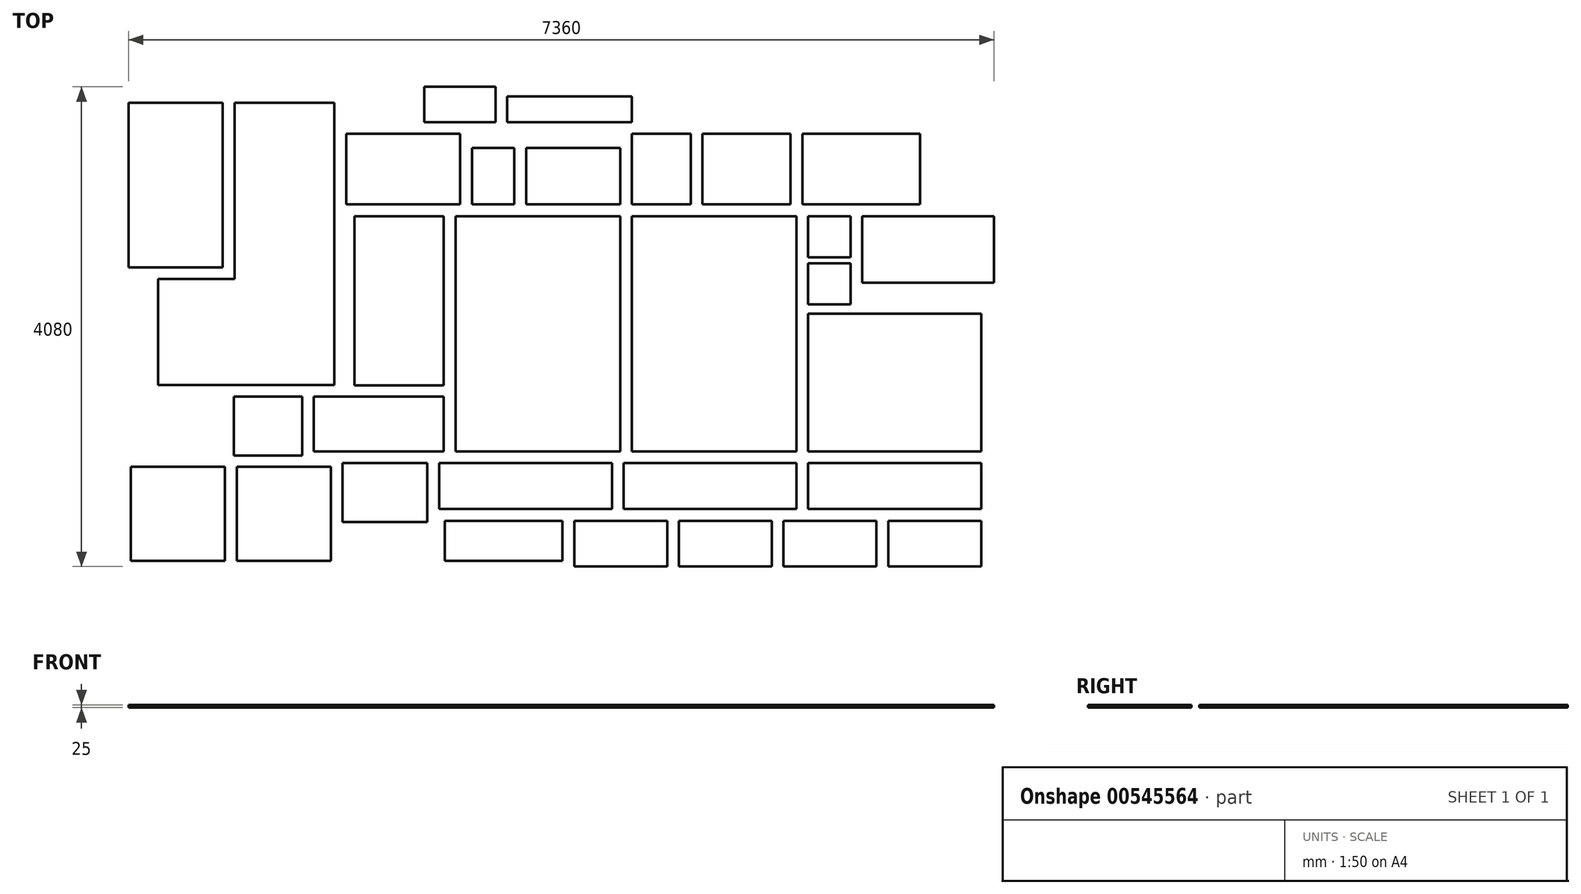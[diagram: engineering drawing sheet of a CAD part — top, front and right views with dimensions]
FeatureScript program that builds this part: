
annotation { "Feature Type Name" : "Feature", "Feature Type Description" : "" }
export const myFeature = defineFeature(function(context is Context, id is Id, definition is map)
    precondition{}
    {
        {
            var Q0;
            Q0=qCreatedBy(makeId("Top.planeOp"),FACE);
            var sketch = newSketch(context, id + "F0", { "sketchPlane" : qUnion([Q0])});
            skLineSegment(sketch, "E0.bottom", {"start": v(0, 0) * mm, "end": v(500, 0) * mm});
            skLineSegment(sketch, "E0.top", {"start": v(0, 600) * mm, "end": v(500, 600) * mm});
            skLineSegment(sketch, "E0.left", {"start": v(0, 0) * mm, "end": v(0, 600) * mm});
            skLineSegment(sketch, "E0.right", {"start": v(500, 0) * mm, "end": v(500, 600) * mm});
            skLineSegment(sketch, "E1.bottom", {"start": v(600, 0) * mm, "end": v(1350, 0) * mm});
            skLineSegment(sketch, "E1.top", {"start": v(600, 600) * mm, "end": v(1350, 600) * mm});
            skLineSegment(sketch, "E1.left", {"start": v(600, 0) * mm, "end": v(600, 600) * mm});
            skLineSegment(sketch, "E1.right", {"start": v(1350, 0) * mm, "end": v(1350, 600) * mm});
            skLineSegment(sketch, "E2.bottom", {"start": v(1450, 0) * mm, "end": v(2450, 0) * mm});
            skLineSegment(sketch, "E2.top", {"start": v(1450, 600) * mm, "end": v(2450, 600) * mm});
            skLineSegment(sketch, "E2.left", {"start": v(1450, 0) * mm, "end": v(1450, 600) * mm});
            skLineSegment(sketch, "E2.right", {"start": v(2450, 0) * mm, "end": v(2450, 600) * mm});
            skLineSegment(sketch, "E3.bottom", {"start": v(0, -100) * mm, "end": v(1400, -100) * mm});
            skLineSegment(sketch, "E3.top", {"start": v(0, -2100) * mm, "end": v(1400, -2100) * mm});
            skLineSegment(sketch, "E3.left", {"start": v(0, -100) * mm, "end": v(0, -2100) * mm});
            skLineSegment(sketch, "E3.right", {"start": v(1400, -100) * mm, "end": v(1400, -2100) * mm});
            skLineSegment(sketch, "E4.bottom", {"start": v(1500, -100) * mm, "end": v(1860, -100) * mm});
            skLineSegment(sketch, "E4.top", {"start": v(1500, -450) * mm, "end": v(1860, -450) * mm});
            skLineSegment(sketch, "E4.left", {"start": v(1500, -100) * mm, "end": v(1500, -450) * mm});
            skLineSegment(sketch, "E4.right", {"start": v(1860, -100) * mm, "end": v(1860, -450) * mm});
            skLineSegment(sketch, "E5.bottom", {"start": v(1500, -500) * mm, "end": v(1860, -500) * mm});
            skLineSegment(sketch, "E5.top", {"start": v(1500, -850) * mm, "end": v(1860, -850) * mm});
            skLineSegment(sketch, "E5.left", {"start": v(1500, -500) * mm, "end": v(1500, -850) * mm});
            skLineSegment(sketch, "E5.right", {"start": v(1860, -500) * mm, "end": v(1860, -850) * mm});
            skLineSegment(sketch, "E6.bottom", {"start": v(-100, -100) * mm, "end": v(-1500, -100) * mm});
            skLineSegment(sketch, "E6.top", {"start": v(-100, -2100) * mm, "end": v(-1500, -2100) * mm});
            skLineSegment(sketch, "E6.left", {"start": v(-100, -100) * mm, "end": v(-100, -2100) * mm});
            skLineSegment(sketch, "E6.right", {"start": v(-1500, -100) * mm, "end": v(-1500, -2100) * mm});
            skLineSegment(sketch, "E7.bottom", {"start": v(1500, -2100) * mm, "end": v(2970, -2100) * mm});
            skLineSegment(sketch, "E7.top", {"start": v(1500, -930) * mm, "end": v(2970, -930) * mm});
            skLineSegment(sketch, "E7.left", {"start": v(1500, -2100) * mm, "end": v(1500, -930) * mm});
            skLineSegment(sketch, "E7.right", {"start": v(2970, -2100) * mm, "end": v(2970, -930) * mm});
            skLineSegment(sketch, "E8.bottom", {"start": v(-100, 480) * mm, "end": v(-900, 480) * mm});
            skLineSegment(sketch, "E8.top", {"start": v(-100, 0) * mm, "end": v(-900, 0) * mm});
            skLineSegment(sketch, "E8.left", {"start": v(-100, 480) * mm, "end": v(-100, 0) * mm});
            skLineSegment(sketch, "E8.right", {"start": v(-900, 480) * mm, "end": v(-900, 0) * mm});
            skLineSegment(sketch, "E9.bottom", {"start": v(-1360, 480) * mm, "end": v(-1000, 480) * mm});
            skLineSegment(sketch, "E9.top", {"start": v(-1360, 0) * mm, "end": v(-1000, 0) * mm});
            skLineSegment(sketch, "E9.left", {"start": v(-1360, 480) * mm, "end": v(-1360, 0) * mm});
            skLineSegment(sketch, "E9.right", {"start": v(-1000, 480) * mm, "end": v(-1000, 0) * mm});
            skLineSegment(sketch, "E10.bottom", {"start": v(-1460, 600) * mm, "end": v(-2430, 600) * mm});
            skLineSegment(sketch, "E10.top", {"start": v(-1460, 0) * mm, "end": v(-2430, 0) * mm});
            skLineSegment(sketch, "E10.left", {"start": v(-1460, 600) * mm, "end": v(-1460, 0) * mm});
            skLineSegment(sketch, "E10.right", {"start": v(-2430, 600) * mm, "end": v(-2430, 0) * mm});
            skLineSegment(sketch, "E11.bottom", {"start": v(-2360, -100) * mm, "end": v(-1600, -100) * mm});
            skLineSegment(sketch, "E11.top", {"start": v(-2360, -1540) * mm, "end": v(-1600, -1540) * mm});
            skLineSegment(sketch, "E11.left", {"start": v(-2360, -100) * mm, "end": v(-2360, -1540) * mm});
            skLineSegment(sketch, "E11.right", {"start": v(-1600, -100) * mm, "end": v(-1600, -1540) * mm});
            skLineSegment(sketch, "E12.bottom", {"start": v(-1600, -2100) * mm, "end": v(-2705, -2100) * mm});
            skLineSegment(sketch, "E12.top", {"start": v(-1600, -1635) * mm, "end": v(-2705, -1635) * mm});
            skLineSegment(sketch, "E12.left", {"start": v(-1600, -2100) * mm, "end": v(-1600, -1635) * mm});
            skLineSegment(sketch, "E12.right", {"start": v(-2705, -2100) * mm, "end": v(-2705, -1635) * mm});
            skLineSegment(sketch, "E13.bottom", {"start": v(0, 920) * mm, "end": v(-1060, 920) * mm});
            skLineSegment(sketch, "E13.top", {"start": v(0, 700) * mm, "end": v(-1060, 700) * mm});
            skLineSegment(sketch, "E13.left", {"start": v(0, 920) * mm, "end": v(0, 700) * mm});
            skLineSegment(sketch, "E13.right", {"start": v(-1060, 920) * mm, "end": v(-1060, 700) * mm});
            skLineSegment(sketch, "E14.bottom", {"start": v(-1765, 1000) * mm, "end": v(-1160, 1000) * mm});
            skLineSegment(sketch, "E14.top", {"start": v(-1765, 700) * mm, "end": v(-1160, 700) * mm});
            skLineSegment(sketch, "E14.left", {"start": v(-1765, 1000) * mm, "end": v(-1765, 700) * mm});
            skLineSegment(sketch, "E14.right", {"start": v(-1160, 1000) * mm, "end": v(-1160, 700) * mm});
            skLineSegment(sketch, "E15.bottom", {"start": v(1960, -100) * mm, "end": v(3080, -100) * mm});
            skLineSegment(sketch, "E15.top", {"start": v(1960, -665) * mm, "end": v(3080, -665) * mm});
            skLineSegment(sketch, "E15.left", {"start": v(1960, -100) * mm, "end": v(1960, -665) * mm});
            skLineSegment(sketch, "E15.right", {"start": v(3080, -100) * mm, "end": v(3080, -665) * mm});
            skLineSegment(sketch, "E16", {"start": v(-2530, -1535) * mm, "end": v(-4030, -1535) * mm});
            skLineSegment(sketch, "E17", {"start": v(-4030, -1535) * mm, "end": v(-4030, -635) * mm});
            skLineSegment(sketch, "E18", {"start": v(-4030, -635) * mm, "end": v(-3380, -635) * mm});
            skLineSegment(sketch, "E19", {"start": v(-3380, -635) * mm, "end": v(-3380, 865) * mm});
            skLineSegment(sketch, "E20", {"start": v(-3380, 865) * mm, "end": v(-2530, 865) * mm});
            skLineSegment(sketch, "E21", {"start": v(-2530, 865) * mm, "end": v(-2530, -1535) * mm});
            skLineSegment(sketch, "E22.bottom", {"start": v(2970, -2200) * mm, "end": v(1500, -2200) * mm});
            skLineSegment(sketch, "E22.top", {"start": v(2970, -2590) * mm, "end": v(1500, -2590) * mm});
            skLineSegment(sketch, "E22.left", {"start": v(2970, -2200) * mm, "end": v(2970, -2590) * mm});
            skLineSegment(sketch, "E22.right", {"start": v(1500, -2200) * mm, "end": v(1500, -2590) * mm});
            skLineSegment(sketch, "E23.bottom", {"start": v(1400, -2200) * mm, "end": v(-70, -2200) * mm});
            skLineSegment(sketch, "E23.top", {"start": v(1400, -2590) * mm, "end": v(-70, -2590) * mm});
            skLineSegment(sketch, "E23.left", {"start": v(1400, -2200) * mm, "end": v(1400, -2590) * mm});
            skLineSegment(sketch, "E23.right", {"start": v(-70, -2200) * mm, "end": v(-70, -2590) * mm});
            skLineSegment(sketch, "E24.bottom", {"start": v(-170, -2200) * mm, "end": v(-1640, -2200) * mm});
            skLineSegment(sketch, "E24.top", {"start": v(-170, -2590) * mm, "end": v(-1640, -2590) * mm});
            skLineSegment(sketch, "E24.left", {"start": v(-170, -2200) * mm, "end": v(-170, -2590) * mm});
            skLineSegment(sketch, "E24.right", {"start": v(-1640, -2200) * mm, "end": v(-1640, -2590) * mm});
            skLineSegment(sketch, "E25.bottom", {"start": v(2970, -2690) * mm, "end": v(2180, -2690) * mm});
            skLineSegment(sketch, "E25.top", {"start": v(2970, -3080) * mm, "end": v(2180, -3080) * mm});
            skLineSegment(sketch, "E25.left", {"start": v(2970, -2690) * mm, "end": v(2970, -3080) * mm});
            skLineSegment(sketch, "E25.right", {"start": v(2180, -2690) * mm, "end": v(2180, -3080) * mm});
            skLineSegment(sketch, "E26.bottom", {"start": v(2080, -2690) * mm, "end": v(1290, -2690) * mm});
            skLineSegment(sketch, "E26.top", {"start": v(2080, -3080) * mm, "end": v(1290, -3080) * mm});
            skLineSegment(sketch, "E26.left", {"start": v(2080, -2690) * mm, "end": v(2080, -3080) * mm});
            skLineSegment(sketch, "E26.right", {"start": v(1290, -2690) * mm, "end": v(1290, -3080) * mm});
            skLineSegment(sketch, "E27.bottom", {"start": v(1190, -2690) * mm, "end": v(400, -2690) * mm});
            skLineSegment(sketch, "E27.top", {"start": v(1190, -3080) * mm, "end": v(400, -3080) * mm});
            skLineSegment(sketch, "E27.left", {"start": v(1190, -2690) * mm, "end": v(1190, -3080) * mm});
            skLineSegment(sketch, "E27.right", {"start": v(400, -2690) * mm, "end": v(400, -3080) * mm});
            skLineSegment(sketch, "E28.bottom", {"start": v(300, -2690) * mm, "end": v(-490, -2690) * mm});
            skLineSegment(sketch, "E28.top", {"start": v(300, -3080) * mm, "end": v(-490, -3080) * mm});
            skLineSegment(sketch, "E28.left", {"start": v(300, -2690) * mm, "end": v(300, -3080) * mm});
            skLineSegment(sketch, "E28.right", {"start": v(-490, -2690) * mm, "end": v(-490, -3080) * mm});
            skLineSegment(sketch, "E29.bottom", {"start": v(-3385, -1635) * mm, "end": v(-2805, -1635) * mm});
            skLineSegment(sketch, "E29.top", {"start": v(-3385, -2135) * mm, "end": v(-2805, -2135) * mm});
            skLineSegment(sketch, "E29.left", {"start": v(-3385, -1635) * mm, "end": v(-3385, -2135) * mm});
            skLineSegment(sketch, "E29.right", {"start": v(-2805, -1635) * mm, "end": v(-2805, -2135) * mm});
            skLineSegment(sketch, "E30.bottom", {"start": v(-1740, -2200) * mm, "end": v(-2460, -2200) * mm});
            skLineSegment(sketch, "E30.top", {"start": v(-1740, -2700) * mm, "end": v(-2460, -2700) * mm});
            skLineSegment(sketch, "E30.left", {"start": v(-1740, -2200) * mm, "end": v(-1740, -2700) * mm});
            skLineSegment(sketch, "E30.right", {"start": v(-2460, -2200) * mm, "end": v(-2460, -2700) * mm});
            skLineSegment(sketch, "E31.bottom", {"start": v(-590, -2690) * mm, "end": v(-1590, -2690) * mm});
            skLineSegment(sketch, "E31.top", {"start": v(-590, -3030) * mm, "end": v(-1590, -3030) * mm});
            skLineSegment(sketch, "E31.left", {"start": v(-590, -2690) * mm, "end": v(-590, -3030) * mm});
            skLineSegment(sketch, "E31.right", {"start": v(-1590, -2690) * mm, "end": v(-1590, -3030) * mm});
            skLineSegment(sketch, "E32.bottom", {"start": v(-2560, -2230) * mm, "end": v(-3360, -2230) * mm});
            skLineSegment(sketch, "E32.top", {"start": v(-2560, -3030) * mm, "end": v(-3360, -3030) * mm});
            skLineSegment(sketch, "E32.left", {"start": v(-2560, -2230) * mm, "end": v(-2560, -3030) * mm});
            skLineSegment(sketch, "E32.right", {"start": v(-3360, -2230) * mm, "end": v(-3360, -3030) * mm});
            skLineSegment(sketch, "E33.bottom", {"start": v(-3460, -2230) * mm, "end": v(-4260, -2230) * mm});
            skLineSegment(sketch, "E33.top", {"start": v(-3460, -3030) * mm, "end": v(-4260, -3030) * mm});
            skLineSegment(sketch, "E33.left", {"start": v(-3460, -2230) * mm, "end": v(-3460, -3030) * mm});
            skLineSegment(sketch, "E33.right", {"start": v(-4260, -2230) * mm, "end": v(-4260, -3030) * mm});
            skLineSegment(sketch, "E34.bottom", {"start": v(-3480, 865) * mm, "end": v(-4280, 865) * mm});
            skLineSegment(sketch, "E34.top", {"start": v(-3480, -535) * mm, "end": v(-4280, -535) * mm});
            skLineSegment(sketch, "E34.left", {"start": v(-3480, 865) * mm, "end": v(-3480, -535) * mm});
            skLineSegment(sketch, "E34.right", {"start": v(-4280, 865) * mm, "end": v(-4280, -535) * mm});
            skSolve(sketch);
        }
        {
            var Q0;
            Q0 = qSketchRegion(id + "F0", true);
            extrude(context, id + "F1", {"entities" : qUnion([Q0]), "depth" : 25 * mm, "offsetDistance" : 25 * mm});
        }
    });
